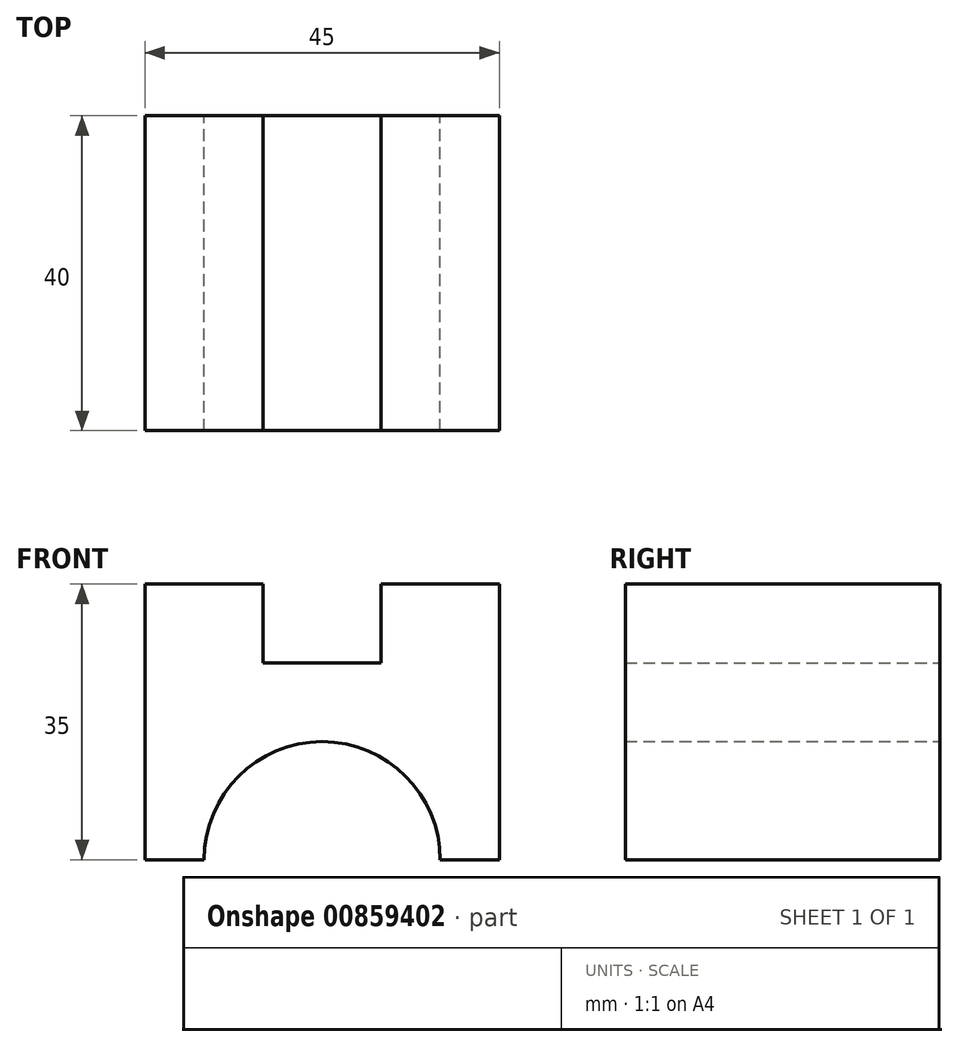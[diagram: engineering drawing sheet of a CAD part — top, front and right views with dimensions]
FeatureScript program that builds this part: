
annotation { "Feature Type Name" : "Feature", "Feature Type Description" : "" }
export const myFeature = defineFeature(function(context is Context, id is Id, definition is map)
    precondition{}
    {
        {
            var Q0;
            Q0=qCreatedBy(makeId("Front.planeOp"),FACE);
            var sketch = newSketch(context, id + "F0", { "sketchPlane" : qUnion([Q0])});
            skLineSegment(sketch, "E0", {"start": v(0, 0) * mm, "end": v(0, 15) * mm});
            skLineSegment(sketch, "E1.bottom", {"start": v(-15, 0) * mm, "end": v(-22.5, 0) * mm});
            skLineSegment(sketch, "E1.top", {"start": v(-7.5, 35) * mm, "end": v(-22.5, 35) * mm});
            skLineSegment(sketch, "E1.right", {"start": v(-22.5, 0) * mm, "end": v(-22.5, 35) * mm});
            skLineSegment(sketch, "E2.bottom", {"start": v(15, 0) * mm, "end": v(22.5, 0) * mm});
            skLineSegment(sketch, "E2.top", {"start": v(7.5, 35) * mm, "end": v(22.5, 35) * mm});
            skLineSegment(sketch, "E2.right", {"start": v(22.5, 0) * mm, "end": v(22.5, 35) * mm});
            skArc(sketch, "E3", {"start": v(15, 0) * mm, "mid": v(0, 15) * mm, "end": v(-15, 0) * mm});
            skLineSegment(sketch, "E4", {"start": v(-22.5, 35) * mm, "end": v(-7.5, 35) * mm});
            skLineSegment(sketch, "E5", {"start": v(22.5, 35) * mm, "end": v(7.5, 35) * mm});
            skLineSegment(sketch, "E6", {"start": v(-7.5, 35) * mm, "end": v(-7.5, 25) * mm});
            skLineSegment(sketch, "E7", {"start": v(-7.5, 25) * mm, "end": v(7.5, 25) * mm});
            skLineSegment(sketch, "E8", {"start": v(7.5, 35) * mm, "end": v(7.5, 25) * mm});
            skSolve(sketch);
        }
        {
            var Q0;
            Q0 = qSketchRegion(id + "F0", true);
            extrude(context, id + "F1", {"entities" : qUnion([Q0]), "depth" : 40 * mm, "offsetDistance" : 25 * mm});
        }
    });
